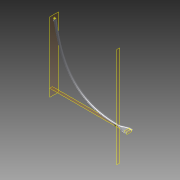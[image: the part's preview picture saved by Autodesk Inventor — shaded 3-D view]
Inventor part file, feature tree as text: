
AUTODESK INVENTOR PART (.ipt)
format: ipt  version: 2012 SP2 (Build 160219200, 219)  size: 239,616 bytes
history: native  units: in
note: dims shown in document units (in); Inventor stores cm internally (conversion verified against a paired STEP export)
features: sketch x7, plane x5, extrude x3, other x2, sweep x1, loft x1
ambient origin geometry x8: Origin, YZ Plane, XZ Plane, XY Plane, X Axis, Y Axis, Z Axis, Center Point
bodies: Solid1 (feature_tree)
feature tree (19):
  sketch  "Sketch1"  dims[d4=0.0in d5=0.3937in]
  plane  "Work Plane1"
  sweep  "Sweep1"
  plane  "Work Plane2"
  extrude  "Extrusion1"  Depth=0.5497in
  plane  "Work Plane3"
  plane  "Work Plane4"
  loft  "Loft1"
  other  "Work Point1"
  plane  "Work Plane5"
  extrude  "Extrusion2"  Depth=0.3937in
  extrude  "Extrusion3"  Depth=2.7559in
  sketch  "Sketch2"  dims[d7=0.5497in d8=0.5497in]
  sketch  "Sketch3"  dims[d9=0.0984in d10=0.7874in]
  sketch  "Sketch4"  dims[d11=0.3937in d12=0.3937in]
  other  "Edges1"
  sketch  "Sketch6"  dims[d19=0.3937in]
  sketch  "Sketch7"  dims[d21=0.7822in d22=0.8495in d23=0.8197in d24=0.5766in d26=90.0deg d29=0.3937in d30=0.0in d31=90.0deg d32=0.5906in d33=0.3937in d34=0.7822in d35=0.8495in d36=0.8197in d37=0.5766in d38=0.0in d39=90.0deg d40=0.5906in d41=0.5512in d42=0.0812in d43=0.0in d44=0.2687in d45=-0.2405in]
  sketch  "Sketch5"  dims[d13=0.0812in d14=0.5094in d15=15.0deg d16=-0.1031in d17=2.7559in]
